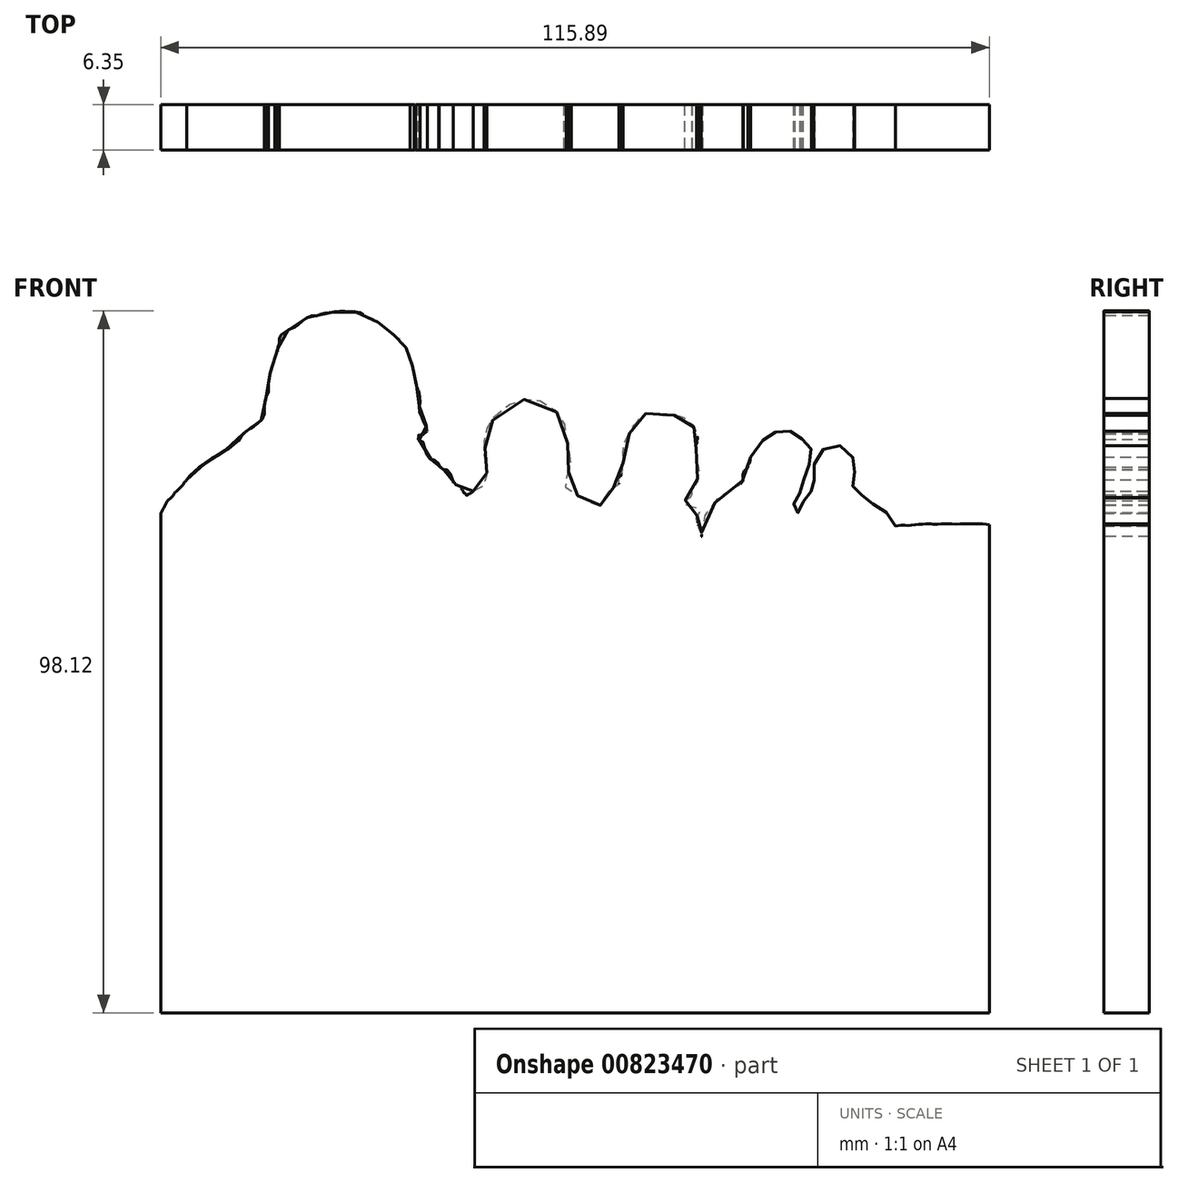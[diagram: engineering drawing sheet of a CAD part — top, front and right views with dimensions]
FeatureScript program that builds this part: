
annotation { "Feature Type Name" : "Feature", "Feature Type Description" : "" }
export const myFeature = defineFeature(function(context is Context, id is Id, definition is map)
    precondition{}
    {
        {
            var Q0;
            Q0=qCreatedBy(makeId("Front.planeOp"),FACE);
            var sketch = newSketch(context, id + "F0", { "sketchPlane" : qUnion([Q0])});
            skLineSegment(sketch, "E0", {"start": v(0, 69.85) * mm, "end": v(0, 0) * mm});
            skLineSegment(sketch, "E1", {"start": v(0, 0) * mm, "end": v(115.89, 0) * mm});
            skLineSegment(sketch, "E2", {"start": v(115.89, 0) * mm, "end": v(115.89, 68.26) * mm});
            skFitSpline(sketch, "E3", {"points": [v(0, 69.85) * mm, v(0.27, 70.35) * mm, v(0.48, 70.74) * mm, v(0.78, 71.27) * mm, v(1.14, 71.76) * mm, v(1.6, 72.18) * mm, v(1.88, 72.57) * mm, v(2.16, 72.89) * mm, v(2.45, 73.13) * mm, v(2.81, 73.48) * mm, v(3.22, 74.01) * mm, v(3.37, 74.24) * mm, v(3.66, 74.55) * mm], "startDerivative": vector(3.09, 5.89) * mm, "endDerivative": vector(4.71, 5.05) * mm});
            skFitSpline(sketch, "E4", {"points": [v(3.66, 74.55) * mm, v(3.79, 74.73) * mm, v(3.97, 74.97) * mm, v(4.1, 75.1) * mm, v(4.42, 75.41) * mm, v(4.74, 75.67) * mm, v(5, 75.95) * mm, v(5.2, 76.08) * mm, v(5.37, 76.24) * mm, v(5.56, 76.27) * mm, v(5.85, 76.54) * mm, v(6.15, 76.78) * mm, v(6.35, 76.96) * mm, v(6.6, 77.16) * mm, v(6.74, 77.25) * mm, v(6.9, 77.27) * mm, v(7.07, 77.42) * mm, v(7.24, 77.6) * mm, v(7.44, 77.7) * mm, v(7.8, 77.85) * mm, v(8.25, 78.12) * mm, v(8.63, 78.36) * mm, v(8.9, 78.6) * mm, v(9.21, 78.72) * mm, v(9.48, 78.84) * mm, v(9.84, 79.12) * mm, v(10.16, 79.44) * mm, v(10.48, 79.67) * mm, v(10.8, 79.87) * mm, v(10.98, 80.07) * mm, v(11.2, 80.23) * mm, v(11.27, 80.48) * mm, v(11.36, 80.8) * mm, v(11.57, 80.99) * mm, v(11.98, 81.3) * mm, v(12.23, 81.45) * mm, v(12.46, 81.64) * mm, v(12.55, 81.77) * mm, v(12.74, 81.86) * mm, v(12.87, 81.98) * mm, v(13, 82.05) * mm, v(13.15, 82.06) * mm, v(13.33, 82.2) * mm, v(13.53, 82.39) * mm, v(13.78, 82.6) * mm, v(13.97, 82.79) * mm, v(14.24, 83.03) * mm, v(14.39, 83.2) * mm, v(14.48, 83.55) * mm, v(14.52, 84.05) * mm, v(14.51, 84.4) * mm, v(14.51, 84.62) * mm, v(14.56, 84.71) * mm, v(14.56, 85) * mm, v(14.57, 85.39) * mm, v(14.65, 85.8) * mm, v(14.74, 86.1) * mm, v(14.8, 86.33) * mm, v(14.92, 86.48) * mm, v(15.03, 86.63) * mm, v(15.04, 87.03) * mm, v(15.06, 87.5) * mm, v(15.06, 87.85) * mm, v(15.03, 88.03) * mm, v(15.1, 88.36) * mm, v(15.13, 88.65) * mm, v(15.2, 89.08) * mm, v(15.3, 89.43) * mm, v(15.34, 89.78) * mm, v(15.43, 90.14) * mm, v(15.56, 90.54) * mm, v(15.84, 91.09) * mm, v(15.98, 91.28) * mm, v(15.98, 91.57) * mm, v(15.99, 91.83) * mm, v(16.16, 92.14) * mm, v(16.3, 92.43) * mm, v(16.39, 92.69) * mm, v(16.39, 92.96) * mm, v(16.52, 93.16) * mm, v(16.61, 93.32) * mm, v(16.6, 93.62) * mm, v(16.61, 93.94) * mm, v(16.61, 94.3) * mm, v(16.68, 94.5) * mm, v(16.8, 94.73) * mm, v(16.93, 94.82) * mm, v(17.07, 94.97) * mm, v(17.3, 95.1) * mm, v(17.58, 95.3) * mm, v(17.84, 95.47) * mm, v(18.03, 95.56) * mm, v(18.16, 95.58) * mm, v(18.23, 95.67) * mm, v(18.41, 95.76) * mm, v(18.54, 95.8) * mm, v(18.71, 95.88) * mm, v(18.9, 96.01) * mm, v(19.07, 96.1) * mm, v(19.3, 96.28) * mm, v(19.71, 96.63) * mm, v(19.99, 96.9) * mm, v(20.36, 97.13) * mm, v(20.68, 97.27) * mm, v(21.04, 97.43) * mm, v(21.33, 97.45) * mm, v(21.76, 97.46) * mm, v(22.1, 97.54) * mm, v(22.5, 97.7) * mm, v(22.7, 97.82) * mm, v(22.87, 97.82) * mm, v(23.1, 97.84) * mm, v(23.4, 97.87) * mm, v(23.7, 97.88) * mm, v(24.04, 97.98) * mm, v(24.32, 98.02) * mm, v(24.6, 98.04) * mm, v(25, 98.07) * mm, v(25.34, 98.11) * mm, v(25.74, 98.11) * mm, v(26.14, 98.09) * mm, v(26.5, 98.04) * mm, v(26.7, 98.05) * mm, v(27.06, 98.02) * mm, v(27.46, 97.9) * mm, v(27.74, 97.88) * mm, v(28.03, 97.82) * mm, v(28.28, 97.6) * mm, v(28.51, 97.5) * mm, v(28.88, 97.37) * mm, v(29.2, 97.27) * mm, v(29.51, 97.15) * mm, v(29.81, 96.95) * mm, v(30.06, 96.79) * mm, v(30.24, 96.69) * mm, v(30.35, 96.56) * mm, v(30.6, 96.38) * mm, v(30.8, 96.2) * mm, v(30.97, 96.07) * mm, v(31.19, 95.92) * mm, v(31.44, 95.66) * mm, v(31.55, 95.51) * mm, v(31.7, 95.38) * mm, v(31.92, 95.24) * mm, v(32, 95.19) * mm, v(32.13, 95.12) * mm, v(32.2, 95) * mm, v(32.3, 94.96) * mm, v(32.44, 94.87) * mm, v(32.54, 94.8) * mm, v(32.6, 94.72) * mm, v(32.75, 94.61) * mm, v(32.94, 94.55) * mm, v(33.04, 94.45) * mm, v(33.2, 94.37) * mm, v(33.4, 94.28) * mm, v(33.48, 94.21) * mm, v(33.56, 94.13) * mm, v(33.65, 93.95) * mm, v(33.8, 93.78) * mm, v(33.92, 93.57) * mm, v(34.03, 93.38) * mm, v(34.1, 93.24) * mm, v(34.24, 93.07) * mm, v(34.37, 92.9) * mm, v(34.46, 92.6) * mm, v(34.6, 92.38) * mm, v(34.7, 92.14) * mm, v(34.72, 92.04) * mm, v(34.75, 91.88) * mm, v(34.84, 91.77) * mm, v(34.85, 91.6) * mm, v(34.88, 91.43) * mm, v(34.97, 91.33) * mm, v(35.02, 91.21) * mm, v(35.08, 91) * mm, v(35.1, 90.8) * mm, v(35.16, 90.53) * mm, v(35.22, 90.32) * mm, v(35.31, 90.07) * mm, v(35.4, 89.8) * mm, v(35.47, 89.53) * mm, v(35.47, 89.36) * mm, v(35.5, 89.14) * mm, v(35.48, 89) * mm, v(35.5, 88.71) * mm, v(35.5, 88.53) * mm, v(35.62, 88.42) * mm, v(35.62, 88.2) * mm, v(35.68, 88.02) * mm, v(35.76, 87.89) * mm, v(35.8, 87.6) * mm, v(35.88, 87.4) * mm, v(35.95, 87.17) * mm, v(36.04, 87.04) * mm, v(36.12, 86.8) * mm, v(36.2, 86.45) * mm, v(36.24, 86.13) * mm, v(36.27, 85.84) * mm, v(36.3, 85.64) * mm, v(36.3, 85.34) * mm, v(36.3, 85.16) * mm, v(36.2, 85.05) * mm, v(36.15, 84.94) * mm, v(36.12, 84.72) * mm, v(36.13, 84.37) * mm, v(36.2, 84.06) * mm, v(36.26, 83.77) * mm, v(36.4, 83.43) * mm, v(36.51, 83.29) * mm, v(36.62, 83.1) * mm, v(36.67, 82.88) * mm, v(36.77, 82.65) * mm, v(36.94, 82.47) * mm, v(37.01, 82.35) * mm, v(37.1, 82.08) * mm, v(37.22, 81.9) * mm, v(37.27, 81.64) * mm, v(37.26, 81.36) * mm, v(37.17, 81.12) * mm, v(36.99, 80.99) * mm, v(36.77, 80.9) * mm, v(36.56, 80.92) * mm, v(36.35, 80.85) * mm, v(36.17, 80.83) * mm, v(35.99, 80.63) * mm, v(35.88, 80.35) * mm, v(35.93, 80.18) * mm, v(36.14, 80.12) * mm, v(36.32, 80.12) * mm, v(36.55, 79.97) * mm, v(36.78, 79.65) * mm, v(36.88, 79.3) * mm, v(36.94, 78.93) * mm, v(37.05, 78.53) * mm, v(37.19, 78.11) * mm, v(37.28, 77.77) * mm, v(37.43, 77.61) * mm, v(37.64, 77.49) * mm, v(37.84, 77.36) * mm, v(38.1, 77.27) * mm, v(38.26, 77.25) * mm, v(38.46, 77.13) * mm, v(38.65, 76.97) * mm, v(38.76, 76.85) * mm, v(38.92, 76.7) * mm, v(38.9, 76.53) * mm, v(38.9, 76.4) * mm, v(39.06, 76.33) * mm, v(39.28, 76.31) * mm, v(39.39, 76.27) * mm, v(39.47, 76.12) * mm, v(39.51, 75.97) * mm, v(39.63, 75.83) * mm, v(39.83, 75.88) * mm, v(40.01, 75.9) * mm, v(40.15, 75.86) * mm, v(40.3, 75.72) * mm, v(40.42, 75.51) * mm, v(40.47, 75.27) * mm, v(40.6, 75.1) * mm, v(40.65, 74.87) * mm, v(40.74, 74.73) * mm, v(40.93, 74.42) * mm, v(40.9, 74.24) * mm, v(41.02, 74.05) * mm, v(41.24, 73.85) * mm, v(41.54, 73.69) * mm, v(41.81, 73.5) * mm, v(41.95, 73.36) * mm, v(42.18, 73.1) * mm, v(42.3, 72.87) * mm, v(42.52, 72.64) * mm, v(42.7, 72.46) * mm, v(42.75, 72.37) * mm, v(43.02, 72.48) * mm, v(43.22, 72.62) * mm, v(43.52, 72.78) * mm, v(43.7, 72.91) * mm], "startDerivative": vector(35.9, 49.58) * mm, "endDerivative": vector(47.06, 40.71) * mm});
            skFitSpline(sketch, "E5", {"points": [v(43.7, 72.91) * mm, v(43.84, 73) * mm, v(44, 73.1) * mm, v(44.2, 73.22) * mm, v(44.35, 73.32) * mm, v(44.58, 73.45) * mm, v(45.01, 73.66) * mm, v(45.21, 73.76) * mm, v(45.32, 73.85) * mm, v(45.43, 73.94) * mm, v(45.5, 74.07) * mm, v(45.56, 74.26) * mm, v(45.59, 74.49) * mm, v(45.62, 74.72) * mm, v(45.6, 75.01) * mm, v(45.6, 75.3) * mm, v(45.59, 75.51) * mm, v(45.59, 75.75) * mm, v(45.57, 75.92) * mm, v(45.55, 76.06) * mm, v(45.56, 76.26) * mm, v(45.51, 76.57) * mm, v(45.5, 76.8) * mm, v(45.44, 76.97) * mm, v(45.4, 77.13) * mm, v(45.35, 77.34) * mm, v(45.3, 77.59) * mm, v(45.26, 77.76) * mm, v(45.25, 78) * mm, v(45.25, 78.2) * mm, v(45.28, 78.44) * mm, v(45.28, 78.68) * mm, v(45.33, 78.97) * mm, v(45.35, 79.32) * mm, v(45.3, 79.69) * mm, v(45.3, 79.96) * mm, v(45.32, 80.25) * mm, v(45.36, 80.54) * mm, v(45.4, 80.88) * mm, v(45.48, 81.1) * mm, v(45.59, 81.32) * mm, v(45.59, 81.54) * mm, v(45.76, 81.87) * mm, v(45.93, 82.17) * mm, v(46.06, 82.43) * mm, v(46.33, 82.72) * mm, v(46.47, 82.97) * mm, v(46.6, 83.24) * mm, v(46.9, 83.62) * mm, v(47.42, 84.19) * mm, v(48.14, 84.6) * mm, v(48.66, 84.94) * mm, v(48.83, 85.1) * mm, v(49.2, 85.28) * mm, v(49.8, 85.46) * mm, v(50.16, 85.63) * mm, v(50.77, 85.75) * mm, v(51.27, 85.86) * mm, v(51.68, 85.9) * mm, v(52.17, 85.89) * mm, v(52.62, 85.79) * mm, v(52.96, 85.63) * mm, v(53.3, 85.52) * mm, v(53.7, 85.34) * mm, v(54.07, 85.04) * mm, v(54.55, 84.73) * mm, v(55, 84.36) * mm, v(55.4, 83.96) * mm, v(55.68, 83.68) * mm, v(55.9, 83.34) * mm, v(56.15, 82.9) * mm, v(56.5, 82.2) * mm, v(56.66, 81.84) * mm, v(56.7, 81.67) * mm, v(56.7, 81.24) * mm, v(56.7, 80.74) * mm, v(56.67, 80.28) * mm, v(56.77, 79.97) * mm, v(56.95, 79.77) * mm, v(56.93, 79.56) * mm, v(56.93, 79.12) * mm, v(56.9, 78.84) * mm, v(56.98, 78.6) * mm, v(57.1, 78.54) * mm, v(57.16, 78.3) * mm, v(57.26, 78) * mm, v(57.36, 77.63) * mm, v(57.4, 77.28) * mm, v(57.37, 76.82) * mm, v(57.28, 76.6) * mm, v(57.2, 76.37) * mm, v(57.16, 76) * mm, v(57.04, 75.66) * mm, v(56.96, 75.41) * mm, v(56.86, 75.13) * mm, v(56.75, 74.9) * mm, v(56.5, 74.68) * mm, v(56.38, 74.6) * mm, v(56.33, 74.4) * mm, v(56.33, 74.1) * mm, v(56.37, 73.86) * mm, v(56.49, 73.61) * mm, v(56.75, 73.3) * mm, v(57.37, 72.82) * mm, v(57.83, 72.57) * mm, v(58.2, 72.36) * mm, v(58.4, 72.28) * mm, v(58.7, 72.1) * mm, v(58.94, 71.93) * mm, v(59.13, 71.9) * mm, v(59.35, 71.85) * mm, v(59.52, 71.7) * mm, v(59.8, 71.57) * mm, v(60.04, 71.4) * mm, v(60.21, 71.31) * mm, v(60.44, 71.18) * mm, v(60.6, 71.04) * mm, v(60.74, 71) * mm, v(60.9, 70.93) * mm, v(61.11, 70.95) * mm, v(61.23, 70.92) * mm, v(61.44, 70.93) * mm, v(61.5, 70.96) * mm, v(61.54, 71.08) * mm, v(61.56, 71.2) * mm, v(61.62, 71.39) * mm, v(61.68, 71.57) * mm, v(61.74, 71.73) * mm, v(61.85, 71.86) * mm, v(62.01, 71.93) * mm, v(62.19, 72.08) * mm, v(62.33, 72.28) * mm, v(62.42, 72.56) * mm, v(62.51, 72.71) * mm, v(62.65, 72.8) * mm, v(62.82, 73.01) * mm, v(62.96, 73.2) * mm, v(63.05, 73.35) * mm, v(63.26, 73.42) * mm, v(63.37, 73.44) * mm, v(63.55, 73.54) * mm, v(63.65, 73.58) * mm, v(63.78, 73.66) * mm, v(64, 73.7) * mm, v(64.1, 73.95) * mm, v(64.1, 74.4) * mm, v(64.1, 74.55) * mm, v(64.1, 74.74) * mm, v(64.25, 75) * mm, v(64.42, 75.18) * mm, v(64.57, 75.3) * mm, v(64.57, 75.66) * mm, v(64.59, 76.3) * mm, v(64.64, 76.76) * mm, v(64.7, 77.03) * mm, v(64.69, 77.39) * mm, v(64.68, 77.77) * mm, v(64.69, 78.17) * mm, v(64.7, 78.8) * mm, v(64.74, 79.24) * mm, v(64.78, 79.48) * mm, v(64.88, 79.65) * mm, v(64.94, 79.85) * mm, v(65.06, 80.18) * mm, v(65.21, 80.53) * mm, v(65.36, 80.76) * mm, v(65.5, 80.95) * mm, v(65.58, 81.14) * mm, v(65.69, 81.37) * mm, v(65.86, 81.6) * mm, v(66.03, 81.86) * mm, v(66.17, 82.11) * mm, v(66.33, 82.31) * mm, v(66.52, 82.54) * mm, v(66.66, 82.67) * mm, v(66.85, 82.89) * mm, v(66.95, 83.02) * mm, v(67.04, 83.18) * mm, v(67.18, 83.37) * mm, v(67.33, 83.52) * mm, v(67.56, 83.69) * mm, v(67.73, 83.74) * mm, v(67.93, 83.79) * mm, v(68.2, 83.8) * mm, v(68.4, 83.8) * mm, v(68.66, 83.78) * mm, v(68.9, 83.73) * mm, v(69.23, 83.68) * mm, v(69.53, 83.66) * mm, v(69.9, 83.6) * mm, v(70.25, 83.56) * mm, v(70.53, 83.54) * mm, v(70.82, 83.54) * mm, v(71.09, 83.53) * mm, v(71.36, 83.53) * mm, v(71.6, 83.53) * mm, v(71.85, 83.5) * mm, v(72.07, 83.46) * mm, v(72.29, 83.43) * mm, v(72.53, 83.41) * mm, v(72.7, 83.4) * mm, v(72.8, 83.34) * mm, v(72.97, 83.27) * mm, v(73.1, 83.22) * mm, v(73.29, 83.12) * mm, v(73.47, 83.03) * mm, v(73.63, 82.86) * mm, v(73.73, 82.73) * mm, v(73.86, 82.58) * mm, v(74.07, 82.47) * mm, v(74.3, 82.26) * mm, v(74.4, 82.1) * mm, v(74.47, 81.95) * mm, v(74.56, 81.88) * mm, v(74.66, 81.8) * mm, v(74.72, 81.62) * mm, v(74.75, 81.48) * mm, v(74.78, 81.3) * mm, v(74.85, 81.18) * mm, v(74.87, 81.04) * mm, v(74.92, 80.86) * mm, v(74.99, 80.71) * mm, v(75.04, 80.51) * mm, v(75.1, 80.3) * mm, v(75.04, 80.15) * mm, v(74.98, 80) * mm, v(74.97, 79.84) * mm, v(74.98, 79.7) * mm, v(74.95, 79.56) * mm, v(74.88, 79.46) * mm, v(74.9, 79.26) * mm, v(74.9, 78.57) * mm, v(74.91, 78.1) * mm, v(74.9, 77.66) * mm, v(74.91, 77.34) * mm, v(74.94, 76.96) * mm, v(75.05, 76.8) * mm, v(75.03, 76.41) * mm, v(75.14, 76.25) * mm, v(75.23, 75.96) * mm, v(75.32, 75.77) * mm, v(75.3, 75.34) * mm, v(75.23, 75.04) * mm, v(75.1, 74.89) * mm, v(75.1, 74.55) * mm, v(75, 74.22) * mm, v(74.82, 73.95) * mm, v(74.73, 73.8) * mm, v(74.66, 73.64) * mm, v(74.55, 73.56) * mm, v(74.41, 73.5) * mm, v(74.3, 73.36) * mm, v(74.28, 73.06) * mm, v(74.3, 72.7) * mm, v(74.25, 72.4) * mm, v(74.14, 72.17) * mm, v(74, 72.01) * mm, v(73.8, 71.8) * mm, v(73.6, 71.72) * mm, v(73.39, 71.67) * mm, v(73.27, 71.51) * mm, v(73.25, 71.12) * mm, v(73.48, 71.02) * mm, v(73.8, 70.93) * mm, v(74.1, 70.85) * mm, v(74.3, 70.8) * mm, v(74.55, 70.71) * mm, v(74.8, 70.66) * mm, v(74.98, 70.48) * mm, v(75.12, 70.37) * mm, v(75.22, 70.21) * mm, v(75.3, 70.07) * mm, v(75.35, 69.98) * mm, v(75.3, 69.84) * mm, v(75.14, 69.64) * mm, v(75, 69.46) * mm, v(74.85, 69.2) * mm, v(74.82, 69.07) * mm, v(74.94, 68.96) * mm, v(75.02, 68.8) * mm, v(75.1, 68.64) * mm, v(75.2, 68.34) * mm, v(75.18, 68) * mm, v(75.24, 67.73) * mm, v(75.35, 67.5) * mm, v(75.53, 67.1) * mm, v(75.64, 66.8) * mm, v(75.7, 66.56) * mm, v(75.75, 66.6) * mm, v(75.72, 66.93) * mm, v(75.62, 67.25) * mm, v(75.59, 67.55) * mm, v(75.72, 67.88) * mm, v(75.83, 68.3) * mm, v(75.98, 68.68) * mm, v(76.06, 69.02) * mm, v(76.14, 69.4) * mm, v(76.27, 69.72) * mm, v(76.54, 70.14) * mm, v(76.74, 70.48) * mm, v(77.07, 70.84) * mm, v(77.32, 71.07) * mm, v(77.5, 71.34) * mm, v(77.7, 71.57) * mm, v(77.85, 71.82) * mm, v(78.22, 72.1) * mm, v(78.6, 72.38) * mm, v(79.08, 72.7) * mm, v(79.77, 73.1) * mm, v(80.09, 73.32) * mm, v(80.52, 73.58) * mm, v(80.9, 73.84) * mm, v(81.23, 74.1) * mm, v(81.35, 74.32) * mm, v(81.43, 74.49) * mm, v(81.46, 74.75) * mm, v(81.44, 75.05) * mm, v(81.47, 75.44) * mm, v(81.58, 75.72) * mm, v(81.7, 75.84) * mm, v(81.85, 75.97) * mm, v(82.02, 76.13) * mm, v(82.12, 76.25) * mm, v(82.14, 76.5) * mm, v(82.16, 76.67) * mm, v(82.29, 76.82) * mm, v(82.36, 76.91) * mm, v(82.4, 76.99) * mm, v(82.41, 77.3) * mm, v(82.5, 77.7) * mm], "startDerivative": vector(58, 39.61) * mm, "endDerivative": vector(29.58, 107.19) * mm});
            skFitSpline(sketch, "E6", {"points": [v(82.5, 77.7) * mm, v(82.6, 77.94) * mm, v(82.75, 78.35) * mm, v(83.17, 79.09) * mm, v(83.59, 79.5) * mm, v(83.85, 79.7) * mm, v(84.15, 79.96) * mm, v(84.49, 80.26) * mm, v(84.85, 80.6) * mm, v(84.98, 80.71) * mm, v(85.14, 80.81) * mm, v(85.26, 80.85) * mm, v(85.47, 80.86) * mm, v(85.6, 80.88) * mm, v(85.94, 81.17) * mm, v(86.01, 81.2) * mm, v(86.18, 81.25) * mm, v(86.41, 81.26) * mm, v(86.57, 81.22) * mm, v(86.66, 81.16) * mm, v(86.96, 81.16) * mm, v(87.19, 81.24) * mm, v(87.54, 81.3) * mm, v(87.8, 81.33) * mm, v(88.02, 81.35) * mm, v(88.21, 81.31) * mm, v(88.5, 81.18) * mm, v(88.66, 81.05) * mm, v(88.84, 80.94) * mm, v(89, 80.81) * mm, v(89.18, 80.72) * mm, v(89.36, 80.52) * mm, v(89.56, 80.32) * mm, v(89.72, 80.2) * mm, v(89.9, 80.12) * mm, v(90, 79.79) * mm, v(90.15, 79.65) * mm, v(90.38, 79.47) * mm, v(90.54, 79.33) * mm, v(90.7, 79.18) * mm, v(90.84, 79.03) * mm, v(90.87, 78.89) * mm, v(91.02, 78.8) * mm, v(91.07, 78.54) * mm, v(91.02, 78.24) * mm, v(91.06, 78.06) * mm, v(91.02, 77.8) * mm, v(90.92, 77.51) * mm, v(90.87, 77.2) * mm, v(90.81, 76.91) * mm, v(90.65, 76.58) * mm, v(90.57, 76.34) * mm, v(90.47, 75.96) * mm, v(90.39, 75.73) * mm, v(90.2, 75.56) * mm, v(90.17, 75.34) * mm, v(90.1, 74.94) * mm, v(89.93, 74.55) * mm, v(89.83, 74.25) * mm, v(89.77, 73.94) * mm, v(89.78, 73.79) * mm, v(89.71, 73.46) * mm, v(89.67, 73.26) * mm, v(89.62, 73.1) * mm, v(89.63, 72.99) * mm, v(89.57, 72.8) * mm, v(89.4, 72.64) * mm, v(89.4, 72.38) * mm, v(89.45, 72.16) * mm, v(89.48, 72.04) * mm, v(89.31, 71.8) * mm, v(89.2, 71.62) * mm, v(89.03, 71.51) * mm, v(88.91, 71.4) * mm, v(88.8, 71.3) * mm, v(88.65, 71.2) * mm, v(88.54, 71.12) * mm, v(88.46, 71.01) * mm, v(88.5, 70.93) * mm, v(88.56, 70.8) * mm, v(88.63, 70.63) * mm, v(88.66, 70.47) * mm, v(88.65, 70.3) * mm, v(88.65, 70.1) * mm, v(88.72, 69.96) * mm, v(88.85, 69.92) * mm, v(89, 69.9) * mm, v(89.2, 69.9) * mm, v(89.34, 70) * mm, v(89.46, 70.13) * mm, v(89.44, 70.33) * mm, v(89.44, 70.52) * mm, v(89.46, 70.85) * mm, v(89.48, 70.99) * mm, v(89.56, 71.11) * mm, v(89.72, 71.3) * mm, v(89.87, 71.45) * mm, v(89.94, 71.56) * mm, v(90.06, 71.57) * mm, v(90.2, 71.64) * mm, v(90.32, 71.82) * mm, v(90.45, 72.05) * mm, v(90.57, 72.27) * mm, v(90.69, 72.43) * mm, v(90.8, 72.6) * mm, v(90.9, 72.79) * mm, v(90.96, 72.91) * mm, v(91.03, 73.13) * mm, v(91.1, 73.28) * mm, v(91.14, 73.4) * mm, v(91.2, 73.6) * mm, v(91.3, 73.7) * mm, v(91.41, 73.82) * mm, v(91.44, 73.88) * mm, v(91.44, 74.03) * mm, v(91.43, 74.2) * mm, v(91.38, 74.43) * mm, v(91.28, 74.63) * mm, v(91.28, 74.91) * mm, v(91.3, 75.18) * mm, v(91.3, 75.43) * mm, v(91.3, 75.7) * mm, v(91.33, 75.95) * mm, v(91.37, 76.24) * mm, v(91.4, 76.7) * mm, v(91.47, 77.12) * mm, v(91.55, 77.43) * mm, v(91.74, 77.7) * mm, v(91.9, 78) * mm, v(92.13, 78.28) * mm, v(92.3, 78.52) * mm, v(92.62, 78.76) * mm, v(92.86, 78.9) * mm, v(93.17, 79.06) * mm, v(93.6, 79.15) * mm, v(93.94, 79.22) * mm, v(94.26, 79.27) * mm, v(94.6, 79.3) * mm, v(94.88, 79.3) * mm, v(95.27, 79.3) * mm, v(95.57, 79.28) * mm, v(95.89, 79.14) * mm, v(96.3, 78.8) * mm, v(96.55, 78.5) * mm, v(96.7, 78.1) * mm, v(96.8, 77.65) * mm, v(96.84, 77.44) * mm, v(96.87, 77.26) * mm, v(96.9, 77.04) * mm, v(96.94, 76.85) * mm, v(96.97, 76.66) * mm, v(96.97, 76.31) * mm, v(96.98, 76.02) * mm, v(97, 75.68) * mm, v(97.04, 75.58) * mm, v(97.04, 75.35) * mm, v(97.02, 75.08) * mm, v(97.02, 74.9) * mm, v(97, 74.75) * mm, v(96.89, 74.71) * mm, v(96.88, 74.46) * mm, v(96.85, 74.1) * mm, v(96.81, 73.76) * mm, v(96.78, 73.56) * mm, v(96.8, 73.4) * mm, v(96.85, 73.26) * mm, v(97, 73.2) * mm, v(97.12, 73.19) * mm, v(97.22, 73.05) * mm, v(97.37, 72.91) * mm, v(97.6, 72.75) * mm, v(97.8, 72.6) * mm, v(98.02, 72.38) * mm, v(98.17, 72.2) * mm, v(98.24, 72.03) * mm, v(98.46, 72.03) * mm, v(98.67, 72.03) * mm, v(98.8, 71.9) * mm, v(98.98, 71.73) * mm, v(99.22, 71.5) * mm, v(99.44, 71.33) * mm, v(99.69, 71.03) * mm, v(99.93, 70.82) * mm, v(100.2, 70.62) * mm, v(100.42, 70.41) * mm, v(100.68, 70.23) * mm, v(100.93, 70.05) * mm, v(101.2, 69.95) * mm, v(101.41, 69.94) * mm, v(101.63, 69.9) * mm, v(101.85, 69.66) * mm, v(102.14, 69.28) * mm, v(102.37, 68.94) * mm, v(102.48, 68.74) * mm, v(102.59, 68.55) * mm, v(102.7, 68.4) * mm, v(102.78, 68.07) * mm], "startDerivative": vector(19.5, 43.77) * mm, "endDerivative": vector(10.62, -60.22) * mm});
            skFitSpline(sketch, "E7", {"points": [v(102.78, 68.07) * mm, v(103.58, 68.16) * mm, v(104, 68.19) * mm, v(104.24, 68.22) * mm, v(104.43, 68.14) * mm, v(104.67, 68.14) * mm, v(105.16, 68.16) * mm, v(105.59, 68.23) * mm, v(105.86, 68.29) * mm, v(106.36, 68.3) * mm, v(106.68, 68.28) * mm, v(106.92, 68.34) * mm, v(107.69, 68.37) * mm, v(107.92, 68.34) * mm, v(108, 68.3) * mm, v(108.37, 68.3) * mm, v(108.9, 68.34) * mm, v(109.2, 68.34) * mm, v(110.12, 68.37) * mm, v(110.67, 68.37) * mm, v(111.27, 68.33) * mm, v(111.73, 68.34) * mm, v(112.22, 68.37) * mm, v(112.9, 68.35) * mm, v(113.53, 68.35) * mm, v(113.83, 68.35) * mm, v(114.38, 68.35) * mm, v(114.94, 68.35) * mm, v(115.33, 68.32) * mm, v(115.6, 68.32) * mm, v(115.89, 68.26) * mm], "startDerivative": vector(18.7, 2.34) * mm, "endDerivative": vector(10.2, -2.82) * mm});
            skSolve(sketch);
        }
        {
            var Q0;
            Q0=makeQuery(id+"F0.imprint","IMPRINT",FACE,{"disambiguationData":[TD([[makeQuery(id+"F0.imprint","IMPRINT",EDGE,{"derivedFrom":sQuery(id+"F0.wireOp",EDGE,"E0")}),1.0]])]});
            extrude(context, id + "F1", {"entities" : qUnion([Q0]), "depth" : 6.35 * mm, "offsetDistance" : 25.4 * mm});
        }
    });
